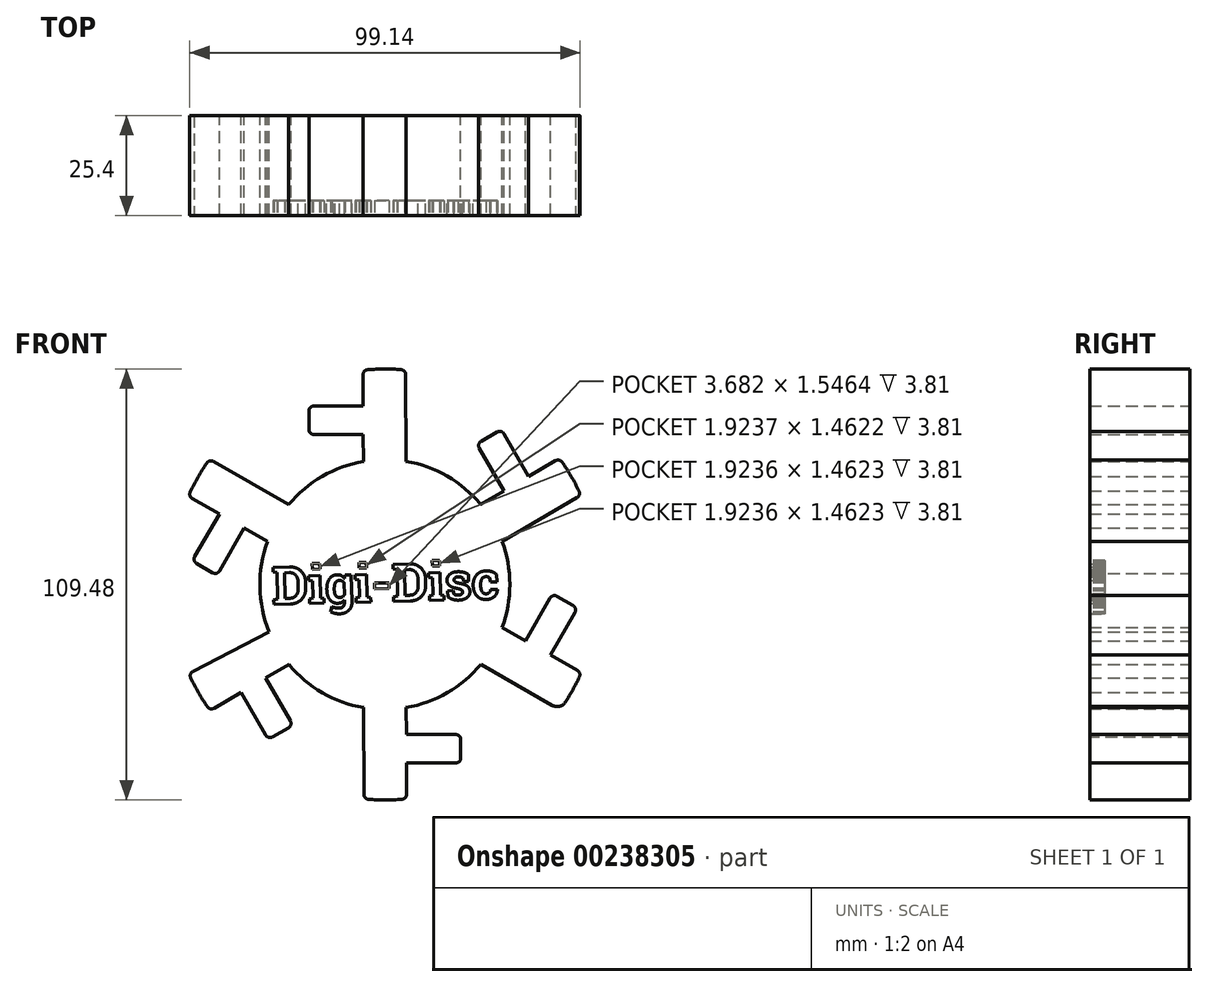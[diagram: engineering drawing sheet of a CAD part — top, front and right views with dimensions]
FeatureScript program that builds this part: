
annotation { "Feature Type Name" : "Feature", "Feature Type Description" : "" }
export const myFeature = defineFeature(function(context is Context, id is Id, definition is map)
    precondition{}
    {
        {
            var Q0;
            Q0=qCreatedBy(makeId("Front.planeOp"),FACE);
            var sketch = newSketch(context, id + "F0", { "sketchPlane" : qUnion([Q0])});
            skArc(sketch, "E0", {"start": v(5.31, 54.48) * mm, "mid": v(-0.12, 54.74) * mm, "end": v(-5.54, 54.46) * mm});
            skCircle(sketch, "E1", {"center": v(0, 0) * mm, "radius": 31.75 * mm});
            skLineSegment(sketch, "E2.left", {"start": v(-5.45, 31.28) * mm, "end": v(-5.48, 38.1) * mm});
            skLineSegment(sketch, "E2.right", {"start": v(5.4, 31.29) * mm, "end": v(5.31, 54.48) * mm});
            skLineSegment(sketch, "E3.bottom", {"start": v(-5.48, 38.1) * mm, "end": v(-19.28, 38.1) * mm});
            skLineSegment(sketch, "E3.top", {"start": v(-5.5, 45.36) * mm, "end": v(-19.28, 45.36) * mm});
            skLineSegment(sketch, "E3.left", {"start": v(5.38, 38.1) * mm, "end": v(5.38, 45.36) * mm});
            skLineSegment(sketch, "E3.right", {"start": v(-19.28, 38.1) * mm, "end": v(-19.28, 45.36) * mm});
            skLineSegment(sketch, "E4.trimOffspring", {"start": v(-5.5, 45.36) * mm, "end": v(-5.54, 54.46) * mm});
            skLineSegment(sketch, "E5.1.0", {"start": v(-30.3, 23.7) * mm, "end": v(-36.6, 27.34) * mm});
            skLineSegment(sketch, "E5.1.1", {"start": v(-24.4, 20.32) * mm, "end": v(-44.53, 31.84) * mm});
            skArc(sketch, "E5.1.2", {"start": v(-44.53, 31.84) * mm, "mid": v(-47.47, 27.27) * mm, "end": v(-49.94, 22.43) * mm});
            skLineSegment(sketch, "E5.1.3", {"start": v(-42.04, 17.9) * mm, "end": v(-49.94, 22.43) * mm});
            skLineSegment(sketch, "E5.1.4", {"start": v(-29.81, 10.92) * mm, "end": v(-35.74, 14.3) * mm});
            skLineSegment(sketch, "E5.1.5", {"start": v(-35.74, 14.3) * mm, "end": v(-42.64, 2.35) * mm});
            skLineSegment(sketch, "E5.1.6", {"start": v(-42.64, 2.35) * mm, "end": v(-48.92, 5.98) * mm});
            skLineSegment(sketch, "E5.1.7", {"start": v(-42.04, 17.9) * mm, "end": v(-48.92, 5.98) * mm});
            skArc(sketch, "E5.2.2", {"start": v(-49.84, -22.64) * mm, "mid": v(-47.35, -27.47) * mm, "end": v(-44.4, -32.03) * mm});
            skLineSegment(sketch, "E5.2.3", {"start": v(-36.53, -27.45) * mm, "end": v(-44.4, -32.03) * mm});
            skLineSegment(sketch, "E5.2.4", {"start": v(-24.36, -20.36) * mm, "end": v(-30.26, -23.8) * mm});
            skLineSegment(sketch, "E5.2.5", {"start": v(-30.26, -23.8) * mm, "end": v(-23.35, -35.75) * mm});
            skLineSegment(sketch, "E5.2.6", {"start": v(-23.35, -35.75) * mm, "end": v(-29.64, -39.38) * mm});
            skLineSegment(sketch, "E5.2.7", {"start": v(-36.53, -27.45) * mm, "end": v(-29.64, -39.38) * mm});
            skLineSegment(sketch, "E5.3.1", {"start": v(-5.4, -31.29) * mm, "end": v(-5.31, -54.48) * mm});
            skArc(sketch, "E5.3.2", {"start": v(-5.31, -54.48) * mm, "mid": v(0.12, -54.74) * mm, "end": v(5.54, -54.46) * mm});
            skLineSegment(sketch, "E5.3.3", {"start": v(5.5, -45.36) * mm, "end": v(5.54, -54.46) * mm});
            skLineSegment(sketch, "E5.3.4", {"start": v(5.45, -31.28) * mm, "end": v(5.48, -38.1) * mm});
            skLineSegment(sketch, "E5.3.5", {"start": v(5.48, -38.1) * mm, "end": v(19.28, -38.1) * mm});
            skLineSegment(sketch, "E5.3.6", {"start": v(19.28, -38.1) * mm, "end": v(19.28, -45.36) * mm});
            skLineSegment(sketch, "E5.3.7", {"start": v(5.5, -45.36) * mm, "end": v(19.28, -45.36) * mm});
            skLineSegment(sketch, "E5.4.0", {"start": v(30.3, -23.7) * mm, "end": v(36.6, -27.34) * mm});
            skLineSegment(sketch, "E5.4.1", {"start": v(24.4, -20.32) * mm, "end": v(44.53, -31.84) * mm});
            skArc(sketch, "E5.4.2", {"start": v(44.53, -31.84) * mm, "mid": v(47.47, -27.27) * mm, "end": v(49.94, -22.43) * mm});
            skLineSegment(sketch, "E5.4.3", {"start": v(42.04, -17.9) * mm, "end": v(49.94, -22.43) * mm});
            skLineSegment(sketch, "E5.4.4", {"start": v(29.81, -10.92) * mm, "end": v(35.74, -14.3) * mm});
            skLineSegment(sketch, "E5.4.5", {"start": v(35.74, -14.3) * mm, "end": v(42.64, -2.35) * mm});
            skLineSegment(sketch, "E5.4.6", {"start": v(42.64, -2.35) * mm, "end": v(48.92, -5.98) * mm});
            skLineSegment(sketch, "E5.4.7", {"start": v(42.04, -17.9) * mm, "end": v(48.92, -5.98) * mm});
            skLineSegment(sketch, "E6.3.5.0", {"start": v(29.8, 10.96) * mm, "end": v(49.84, 22.64) * mm});
            skArc(sketch, "E6.6.5.0", {"start": v(49.84, 22.64) * mm, "mid": v(47.35, 27.47) * mm, "end": v(44.4, 32.03) * mm});
            skLineSegment(sketch, "E6.10.5.0", {"start": v(36.53, 27.45) * mm, "end": v(44.4, 32.03) * mm});
            skLineSegment(sketch, "E6.13.5.0", {"start": v(24.36, 20.36) * mm, "end": v(30.26, 23.8) * mm});
            skLineSegment(sketch, "E6.16.5.0", {"start": v(30.26, 23.8) * mm, "end": v(23.35, 35.75) * mm});
            skLineSegment(sketch, "E6.19.5.0", {"start": v(23.35, 35.75) * mm, "end": v(29.64, 39.38) * mm});
            skLineSegment(sketch, "E6.22.5.0", {"start": v(36.53, 27.45) * mm, "end": v(29.64, 39.38) * mm});
            skLineSegment(sketch, "E7", {"start": v(-49.84, -22.64) * mm, "end": v(-29.37, -12.07) * mm});
            skSolve(sketch);
        }
        {
            var Q0;
            {var subQ0=sQuery(id+"F0.wireOp",EDGE,"E1");var subQ5=makeQuery(id+"F0.imprint","INTERSECT",VERTEX,{"derivedFrom":[subQ0,sQuery(id+"F0.wireOp",EDGE,"E5.4.1")]});Q0=makeQuery(id+"F0.imprint","IMPRINT",FACE,{"disambiguationData":[TD([[makeQuery(id+"F0.imprint","IMPRINT",EDGE,{"disambiguationData":[TD([[subQ5,-1.0]])],"derivedFrom":subQ0}),1.0]])]});}
            var Q1;
            {var subQ0=sQuery(id+"F0.wireOp",EDGE,"E5.1.2");Q1=makeQuery(id+"F0.imprint","IMPRINT",FACE,{"disambiguationData":[TD([[makeQuery(id+"F0.imprint","IMPRINT",EDGE,{"derivedFrom":subQ0}),1.0]])]});}
            var Q2;
            {var subQ5=sQuery(id+"F0.wireOp",EDGE,"E0");Q2=makeQuery(id+"F0.imprint","IMPRINT",FACE,{"disambiguationData":[TD([[makeQuery(id+"F0.imprint","IMPRINT",EDGE,{"derivedFrom":subQ5}),1.0]])]});}
            var Q3;
            {var subQ0=sQuery(id+"F0.wireOp",EDGE,"E5.4.2");Q3=makeQuery(id+"F0.imprint","IMPRINT",FACE,{"disambiguationData":[TD([[makeQuery(id+"F0.imprint","IMPRINT",EDGE,{"derivedFrom":subQ0}),1.0]])]});}
            var Q4;
            {var subQ0=sQuery(id+"F0.wireOp",EDGE,"E5.3.2");Q4=makeQuery(id+"F0.imprint","IMPRINT",FACE,{"disambiguationData":[TD([[makeQuery(id+"F0.imprint","IMPRINT",EDGE,{"derivedFrom":subQ0}),1.0]])]});}
            var Q5;
            {var subQ0=sQuery(id+"F0.wireOp",EDGE,"E5.2.2");Q5=makeQuery(id+"F0.imprint","IMPRINT",FACE,{"disambiguationData":[TD([[makeQuery(id+"F0.imprint","IMPRINT",EDGE,{"derivedFrom":subQ0}),1.0]])]});}
            var Q6;
            {var subQ0=sQuery(id+"F0.wireOp",EDGE,"E6.6.5.0");Q6=makeQuery(id+"F0.imprint","IMPRINT",FACE,{"disambiguationData":[TD([[makeQuery(id+"F0.imprint","IMPRINT",EDGE,{"derivedFrom":subQ0}),1.0]])]});}
            extrude(context, id + "F1", {"entities" : qUnion([Q0, Q1, Q2, Q3, Q4, Q5, Q6]), "depth" : 25.4 * mm, "offsetDistance" : 25.4 * mm});
        }
        {
            var Q0;
            Q0=makeQuery(id+"F1.opExtrude","SWEPT_EDGE",EDGE,{"disambiguationData":[OSD([sQuery(id+"F0.wireOp",EDGE,"E0"),sQuery(id+"F0.wireOp",EDGE,"E2.right")])]});
            var Q1;
            Q1=makeQuery(id+"F1.opExtrude","SWEPT_EDGE",EDGE,{"disambiguationData":[OSD([sQuery(id+"F0.wireOp",EDGE,"E0"),sQuery(id+"F0.wireOp",EDGE,"E4.trimOffspring")])]});
            fillet(context, id + "F2", {"entities" : qUnion([Q0, Q1]), "radius" : 1.27 * mm, "tangentPropagation" : true, "allowEdgeOverflow" : false});
        }
        {
            var Q0;
            Q0=makeQuery(id+"F1.opExtrude","SWEPT_EDGE",EDGE,{"disambiguationData":[OSD([sQuery(id+"F0.wireOp",EDGE,"E3.top"),sQuery(id+"F0.wireOp",EDGE,"E3.right")])]});
            var Q1;
            Q1=makeQuery(id+"F1.opExtrude","SWEPT_EDGE",EDGE,{"disambiguationData":[OSD([sQuery(id+"F0.wireOp",EDGE,"E3.bottom"),sQuery(id+"F0.wireOp",EDGE,"E3.right")])]});
            fillet(context, id + "F3", {"entities" : qUnion([Q0, Q1]), "radius" : 1.27 * mm, "tangentPropagation" : true, "allowEdgeOverflow" : false});
        }
        {
            var Q0;
            Q0=makeQuery(id+"F1.opExtrude","SWEPT_EDGE",EDGE,{"disambiguationData":[OSD([sQuery(id+"F0.wireOp",EDGE,"E6.19.5.0"),sQuery(id+"F0.wireOp",EDGE,"E6.22.5.0")])]});
            var Q1;
            Q1=makeQuery(id+"F1.opExtrude","SWEPT_EDGE",EDGE,{"disambiguationData":[OSD([sQuery(id+"F0.wireOp",EDGE,"E6.16.5.0"),sQuery(id+"F0.wireOp",EDGE,"E6.19.5.0")])]});
            var Q2;
            Q2=makeQuery(id+"F1.opExtrude","SWEPT_EDGE",EDGE,{"disambiguationData":[OSD([sQuery(id+"F0.wireOp",EDGE,"E6.6.5.0"),sQuery(id+"F0.wireOp",EDGE,"E6.10.5.0")])]});
            var Q3;
            Q3=makeQuery(id+"F1.opExtrude","SWEPT_EDGE",EDGE,{"disambiguationData":[OSD([sQuery(id+"F0.wireOp",EDGE,"E6.3.5.0"),sQuery(id+"F0.wireOp",EDGE,"E6.6.5.0")])]});
            var Q4;
            Q4=makeQuery(id+"F1.opExtrude","SWEPT_EDGE",EDGE,{"disambiguationData":[OSD([sQuery(id+"F0.wireOp",EDGE,"E5.4.6"),sQuery(id+"F0.wireOp",EDGE,"E5.4.7")])]});
            var Q5;
            Q5=makeQuery(id+"F1.opExtrude","SWEPT_EDGE",EDGE,{"disambiguationData":[OSD([sQuery(id+"F0.wireOp",EDGE,"E5.4.2"),sQuery(id+"F0.wireOp",EDGE,"E5.4.3")])]});
            var Q6;
            Q6=makeQuery(id+"F1.opExtrude","SWEPT_EDGE",EDGE,{"disambiguationData":[OSD([sQuery(id+"F0.wireOp",EDGE,"E5.4.5"),sQuery(id+"F0.wireOp",EDGE,"E5.4.6")])]});
            var Q7;
            Q7=makeQuery(id+"F1.opExtrude","SWEPT_EDGE",EDGE,{"disambiguationData":[OSD([sQuery(id+"F0.wireOp",EDGE,"E5.3.6"),sQuery(id+"F0.wireOp",EDGE,"E5.3.7")])]});
            var Q8;
            Q8=makeQuery(id+"F1.opExtrude","SWEPT_EDGE",EDGE,{"disambiguationData":[OSD([sQuery(id+"F0.wireOp",EDGE,"E5.3.5"),sQuery(id+"F0.wireOp",EDGE,"E5.3.6")])]});
            var Q9;
            Q9=makeQuery(id+"F1.opExtrude","SWEPT_EDGE",EDGE,{"disambiguationData":[OSD([sQuery(id+"F0.wireOp",EDGE,"E5.3.2"),sQuery(id+"F0.wireOp",EDGE,"E5.3.3")])]});
            var Q10;
            Q10=makeQuery(id+"F1.opExtrude","SWEPT_EDGE",EDGE,{"disambiguationData":[OSD([sQuery(id+"F0.wireOp",EDGE,"E5.3.1"),sQuery(id+"F0.wireOp",EDGE,"E5.3.2")])]});
            var Q11;
            Q11=makeQuery(id+"F1.opExtrude","SWEPT_EDGE",EDGE,{"disambiguationData":[OSD([sQuery(id+"F0.wireOp",EDGE,"E5.2.6"),sQuery(id+"F0.wireOp",EDGE,"E5.2.7")])]});
            var Q12;
            Q12=makeQuery(id+"F1.opExtrude","SWEPT_EDGE",EDGE,{"disambiguationData":[OSD([sQuery(id+"F0.wireOp",EDGE,"E5.2.5"),sQuery(id+"F0.wireOp",EDGE,"E5.2.6")])]});
            var Q13;
            Q13=makeQuery(id+"F1.opExtrude","SWEPT_EDGE",EDGE,{"disambiguationData":[OSD([sQuery(id+"F0.wireOp",EDGE,"E5.2.2"),sQuery(id+"F0.wireOp",EDGE,"E5.2.3")])]});
            var Q14;
            Q14=makeQuery(id+"F1.opExtrude","SWEPT_EDGE",EDGE,{"disambiguationData":[OSD([sQuery(id+"F0.wireOp",EDGE,"E5.2.1"),sQuery(id+"F0.wireOp",EDGE,"E5.2.2")])]});
            var Q15;
            Q15=makeQuery(id+"F1.opExtrude","SWEPT_EDGE",EDGE,{"disambiguationData":[OSD([sQuery(id+"F0.wireOp",EDGE,"E5.1.6"),sQuery(id+"F0.wireOp",EDGE,"E5.1.7")])]});
            var Q16;
            Q16=makeQuery(id+"F1.opExtrude","SWEPT_EDGE",EDGE,{"disambiguationData":[OSD([sQuery(id+"F0.wireOp",EDGE,"E5.1.5"),sQuery(id+"F0.wireOp",EDGE,"E5.1.6")])]});
            var Q17;
            Q17=makeQuery(id+"F1.opExtrude","SWEPT_EDGE",EDGE,{"disambiguationData":[OSD([sQuery(id+"F0.wireOp",EDGE,"E5.1.2"),sQuery(id+"F0.wireOp",EDGE,"E5.1.3")])]});
            var Q18;
            Q18=makeQuery(id+"F1.opExtrude","SWEPT_EDGE",EDGE,{"disambiguationData":[OSD([sQuery(id+"F0.wireOp",EDGE,"E5.1.1"),sQuery(id+"F0.wireOp",EDGE,"E5.1.2")])]});
            fillet(context, id + "F4", {"entities" : qUnion([Q0, Q1, Q2, Q3, Q4, Q5, Q6, Q7, Q8, Q9, Q10, Q11, Q12, Q13, Q14, Q15, Q16, Q17, Q18]), "radius" : 1.27 * mm, "tangentPropagation" : true, "allowEdgeOverflow" : false});
        }
        {
            var Q0;
            Q0=makeQuery(id+"F1.opExtrude","SWEPT_EDGE",EDGE,{"disambiguationData":[OSD([sQuery(id+"F0.wireOp",EDGE,"E5.4.1"),sQuery(id+"F0.wireOp",EDGE,"E5.4.2")])]});
            fillet(context, id + "F5", {"entities" : qUnion([Q0]), "radius" : 2.54 * mm, "tangentPropagation" : true, "allowEdgeOverflow" : false});
        }
        {
            var Q0;
            Q0=makeQuery(id+"F1.opExtrude","CAP_FACE",FACE,{"disambiguationData":[OSD([sQuery(id+"F0.wireOp",EDGE,"E0"),sQuery(id+"F0.wireOp",EDGE,"E1"),sQuery(id+"F0.wireOp",EDGE,"E2.left"),sQuery(id+"F0.wireOp",EDGE,"E2.right"),sQuery(id+"F0.wireOp",EDGE,"E3.bottom"),sQuery(id+"F0.wireOp",EDGE,"E3.top"),sQuery(id+"F0.wireOp",EDGE,"E3.right"),sQuery(id+"F0.wireOp",EDGE,"E4.trimOffspring"),sQuery(id+"F0.wireOp",EDGE,"E5.1.1"),sQuery(id+"F0.wireOp",EDGE,"E5.1.2"),sQuery(id+"F0.wireOp",EDGE,"E5.1.3"),sQuery(id+"F0.wireOp",EDGE,"E5.1.4"),sQuery(id+"F0.wireOp",EDGE,"E5.1.5"),sQuery(id+"F0.wireOp",EDGE,"E5.1.6"),sQuery(id+"F0.wireOp",EDGE,"E5.1.7"),sQuery(id+"F0.wireOp",EDGE,"E5.2.2"),sQuery(id+"F0.wireOp",EDGE,"E5.2.3"),sQuery(id+"F0.wireOp",EDGE,"E5.2.4"),sQuery(id+"F0.wireOp",EDGE,"E5.2.5"),sQuery(id+"F0.wireOp",EDGE,"E5.2.6"),sQuery(id+"F0.wireOp",EDGE,"E5.2.7"),sQuery(id+"F0.wireOp",EDGE,"E5.3.1"),sQuery(id+"F0.wireOp",EDGE,"E5.3.2"),sQuery(id+"F0.wireOp",EDGE,"E5.3.3"),sQuery(id+"F0.wireOp",EDGE,"E5.3.4"),sQuery(id+"F0.wireOp",EDGE,"E5.3.5"),sQuery(id+"F0.wireOp",EDGE,"E5.3.6"),sQuery(id+"F0.wireOp",EDGE,"E5.3.7"),sQuery(id+"F0.wireOp",EDGE,"E5.4.1"),sQuery(id+"F0.wireOp",EDGE,"E5.4.2"),sQuery(id+"F0.wireOp",EDGE,"E5.4.3"),sQuery(id+"F0.wireOp",EDGE,"E5.4.4"),sQuery(id+"F0.wireOp",EDGE,"E5.4.5"),sQuery(id+"F0.wireOp",EDGE,"E5.4.6"),sQuery(id+"F0.wireOp",EDGE,"E5.4.7"),sQuery(id+"F0.wireOp",EDGE,"E6.3.5.0"),sQuery(id+"F0.wireOp",EDGE,"E6.6.5.0"),sQuery(id+"F0.wireOp",EDGE,"E6.10.5.0"),sQuery(id+"F0.wireOp",EDGE,"E6.13.5.0"),sQuery(id+"F0.wireOp",EDGE,"E6.16.5.0"),sQuery(id+"F0.wireOp",EDGE,"E6.19.5.0"),sQuery(id+"F0.wireOp",EDGE,"E6.22.5.0"),sQuery(id+"F0.wireOp",EDGE,"E7")])],"isStart":false});
            var sketch = newSketch(context, id + "F6", { "sketchPlane" : qUnion([Q0])});
            skText(sketch, "E8", { "text": "Digi-Disc ", "fontName": "RobotoSlab-Bold.ttf"});
            const initialGuessF6  = {"E8": [-0.02855, -0.00506, 0.99968, 0.02548, 0.00953]};
            skSetInitialGuess(sketch, initialGuessF6);
            skSolve(sketch);
        }
        {
            var Q0;
            Q0=makeQuery(id+"F6.imprint","IMPRINT",FACE,{"disambiguationData":[TD([[makeQuery(id+"F6.imprint","IMPRINT",EDGE,{"derivedFrom":sQuery(id+"F6.wireOp",EDGE,"E8.sketch_text.stroke-0")}),-1.0]])]});
            var Q1;
            Q1=makeQuery(id+"F6.imprint","IMPRINT",FACE,{"disambiguationData":[TD([[makeQuery(id+"F6.imprint","IMPRINT",EDGE,{"derivedFrom":sQuery(id+"F6.wireOp",EDGE,"E8.sketch_text.stroke-21")}),-1.0]])]});
            var Q2;
            Q2=makeQuery(id+"F6.imprint","IMPRINT",FACE,{"disambiguationData":[TD([[makeQuery(id+"F6.imprint","IMPRINT",EDGE,{"derivedFrom":sQuery(id+"F6.wireOp",EDGE,"E8.sketch_text.stroke-31")}),-1.0]])]});
            var Q3;
            Q3=makeQuery(id+"F6.imprint","IMPRINT",FACE,{"disambiguationData":[TD([[makeQuery(id+"F6.imprint","IMPRINT",EDGE,{"derivedFrom":sQuery(id+"F6.wireOp",EDGE,"E8.sketch_text.stroke-35")}),-1.0]])]});
            var Q4;
            Q4=makeQuery(id+"F6.imprint","IMPRINT",FACE,{"disambiguationData":[TD([[makeQuery(id+"F6.imprint","IMPRINT",EDGE,{"derivedFrom":sQuery(id+"F6.wireOp",EDGE,"E8.sketch_text.stroke-67")}),-1.0]])]});
            var Q5;
            Q5=makeQuery(id+"F6.imprint","IMPRINT",FACE,{"disambiguationData":[TD([[makeQuery(id+"F6.imprint","IMPRINT",EDGE,{"derivedFrom":sQuery(id+"F6.wireOp",EDGE,"E8.sketch_text.stroke-77")}),-1.0]])]});
            var Q6;
            Q6=makeQuery(id+"F6.imprint","IMPRINT",FACE,{"disambiguationData":[TD([[makeQuery(id+"F6.imprint","IMPRINT",EDGE,{"derivedFrom":sQuery(id+"F6.wireOp",EDGE,"E8.sketch_text.stroke-81")}),-1.0]])]});
            var Q7;
            Q7=makeQuery(id+"F6.imprint","IMPRINT",FACE,{"disambiguationData":[TD([[makeQuery(id+"F6.imprint","IMPRINT",EDGE,{"derivedFrom":sQuery(id+"F6.wireOp",EDGE,"E8.sketch_text.stroke-85")}),-1.0]])]});
            var Q8;
            Q8=makeQuery(id+"F6.imprint","IMPRINT",FACE,{"disambiguationData":[TD([[makeQuery(id+"F6.imprint","IMPRINT",EDGE,{"derivedFrom":sQuery(id+"F6.wireOp",EDGE,"E8.sketch_text.stroke-106")}),-1.0]])]});
            var Q9;
            Q9=makeQuery(id+"F6.imprint","IMPRINT",FACE,{"disambiguationData":[TD([[makeQuery(id+"F6.imprint","IMPRINT",EDGE,{"derivedFrom":sQuery(id+"F6.wireOp",EDGE,"E8.sketch_text.stroke-116")}),-1.0]])]});
            var Q10;
            Q10=makeQuery(id+"F6.imprint","IMPRINT",FACE,{"disambiguationData":[TD([[makeQuery(id+"F6.imprint","IMPRINT",EDGE,{"derivedFrom":sQuery(id+"F6.wireOp",EDGE,"E8.sketch_text.stroke-120")}),-1.0]])]});
            var Q11;
            Q11=makeQuery(id+"F6.imprint","IMPRINT",FACE,{"disambiguationData":[TD([[makeQuery(id+"F6.imprint","IMPRINT",EDGE,{"derivedFrom":sQuery(id+"F6.wireOp",EDGE,"E8.sketch_text.stroke-150")}),-1.0]])]});
            extrude(context, id + "F7", {"entities" : qUnion([Q0, Q1, Q2, Q3, Q4, Q5, Q6, Q7, Q8, Q9, Q10, Q11]), "operationType" : NewBodyOperationType.REMOVE, "oppositeDirection" : true, "depth" : 3.8 * mm, "offsetDistance" : 25.4 * mm});
        }
    });
